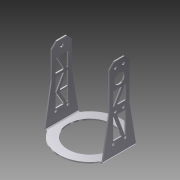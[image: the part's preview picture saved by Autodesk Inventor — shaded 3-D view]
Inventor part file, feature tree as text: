
AUTODESK INVENTOR PART (.ipt)
format: ipt  version: 2016 SP1 (Build 200210100, 210)  size: 636,928 bytes
history: native  units: in
note: dims shown in document units (in); Inventor stores cm internally (conversion verified against a paired STEP export)
features: sketch x17, other x14, extrude x4, sheet_metal_op x4, projected_geometry x3, fillet x2, plane x2, reference x2, mirror x1
ambient origin geometry x8: Origin, YZ Plane, XZ Plane, XY Plane, X Axis, Y Axis, Z Axis, Center Point
bodies: Solid1 (feature_tree)
feature tree (49):
  extrude  "Extrusion1"  Depth=2.2in
  extrude  "Extrusion2"  Depth=0.0625in
  sheet_metal_op  "Bend1"
  sheet_metal_op  "Bend2"
  fillet  "Fillet1"  Radius=0.116in
  sketch  "Sketch12"  dims[d21=0.0625in]
  extrude  "Extrusion3"  Depth=0.0625in
  sheet_metal_op  "Bend3"
  extrude  "Extrusion4"  Depth=2.808in
  sheet_metal_op  "Bend4"
  fillet  "Fillet2"  Radius=0.0625in
  plane  "Work Plane1"
  mirror  "Mirror1"
  plane  "Work Plane2"
  sketch  "Sketch1"  dims[d0=3.1in d1=2.2in]
  sketch  "Sketch2"  dims[d2=0.0625in d3=0.0in d4=2.4in d5=0.116in]
  sketch  "Sketch3"  dims[d6=2.3622in d8=360.0deg d10=0.0625in]
  sketch  "Sketch4"  dims[d11=0.0in d12=2.808in d13=0.0625in]
  sketch  "Sketch5"  dims[d14=0.0in]
  sketch  "Sketch6"  dims[d15=1.0in]
  sketch  "Sketch7"  dims[d16=1.0in]
  sketch  "Sketch8"  dims[d17=0.0625in]
  sketch  "Sketch9"  dims[d18=0.0625in]
  reference  "Reference1"
  sketch  "Sketch10"  dims[d19=4.0875in d20=0.0in]
  sketch  "Sketch13"  dims[d22=0.0312in]
  projected_geometry  "Projected Loop1"
  projected_geometry  "Projected Loop2"
  sketch  "Sketch14"  dims[d23=0.125in]
  projected_geometry  "Projected Loop3"
  reference  "Reference2"
  sketch  "Sketch19"  dims[d24=0.0625in]
  sketch  "Sketch21"  dims[d25=0.0625in]
  sketch  "Sketch22"  dims[d26=0.0625in]
  sketch  "Sketch23"  dims[d27=0.0312in d28=0.125in d29=0.0625in d30=0.0625in d31=0.0625in d32=0.0in d33=0.0312in d34=3.305in d35=0.51in d36=0.0625in d37=0.0in d38=1.8819in d39=0.4016in d40=0.5829in d41=0.1181in d42=0.0625in d43=0.0in d44=0.617in d45=0.6in d46=0.1181in d47=0.0625in d48=0.0in d49=0.0625in d50=0.0in d51=0.3in d52=0.25in d53=0.25in d54=0.25in d55=0.25in d56=0.25in d57=0.25in d58=0.25in d59=0.25in d60=0.0625in d61=0.0in d62=0.1875in d63=0.1875in d88=0.0312in d93=0.0625in d94=0.0in d95=0.0625in d96=0.0in d97=0.125in d98=0.0625in d99=0.0625in d100=0.0625in d101=0.0in d102=0.0625in d103=0.0in d104=0.125in d105=0.0625in d106=0.0625in d107=0.125in d132=0.5079in d133=0.1695in d134=0.0625in d135=0.0in d139=2.906in d142=0.312in d144=0.031in d145=0.031in d146=2.22in d148=0.062in d150=0.312in d151=0.066in d152=0.0625in d153=0.0in d154=-0.0625in d155=-0.05in d160=0.031in d161=0.031in d162=0.72in d163=1.358in d164=0.0625in d165=0.0in d166=2.9063in d167=2.22in d168=0.312in d169=0.312in d170=0.0662in d171=0.0625in d172=0.0in d173=0.031in d174=1.81in d175=0.748in d177=0.031in d178=0.082in d179=0.031in d180=0.0625in d181=0.0in]
  other  "Cut1"
  other  "Cut2"
  other  "Cut3"
  other  "Cut4"
  other  "Cut5"
  other  "Cut6"
  other  "Cut7"
  other  "Cut8"
  other  "Cut13"
  other  "Cut14"
  other  "Cut15"
  other  "Cut16"
  other  "Cut17"
  other  "Definition1"
